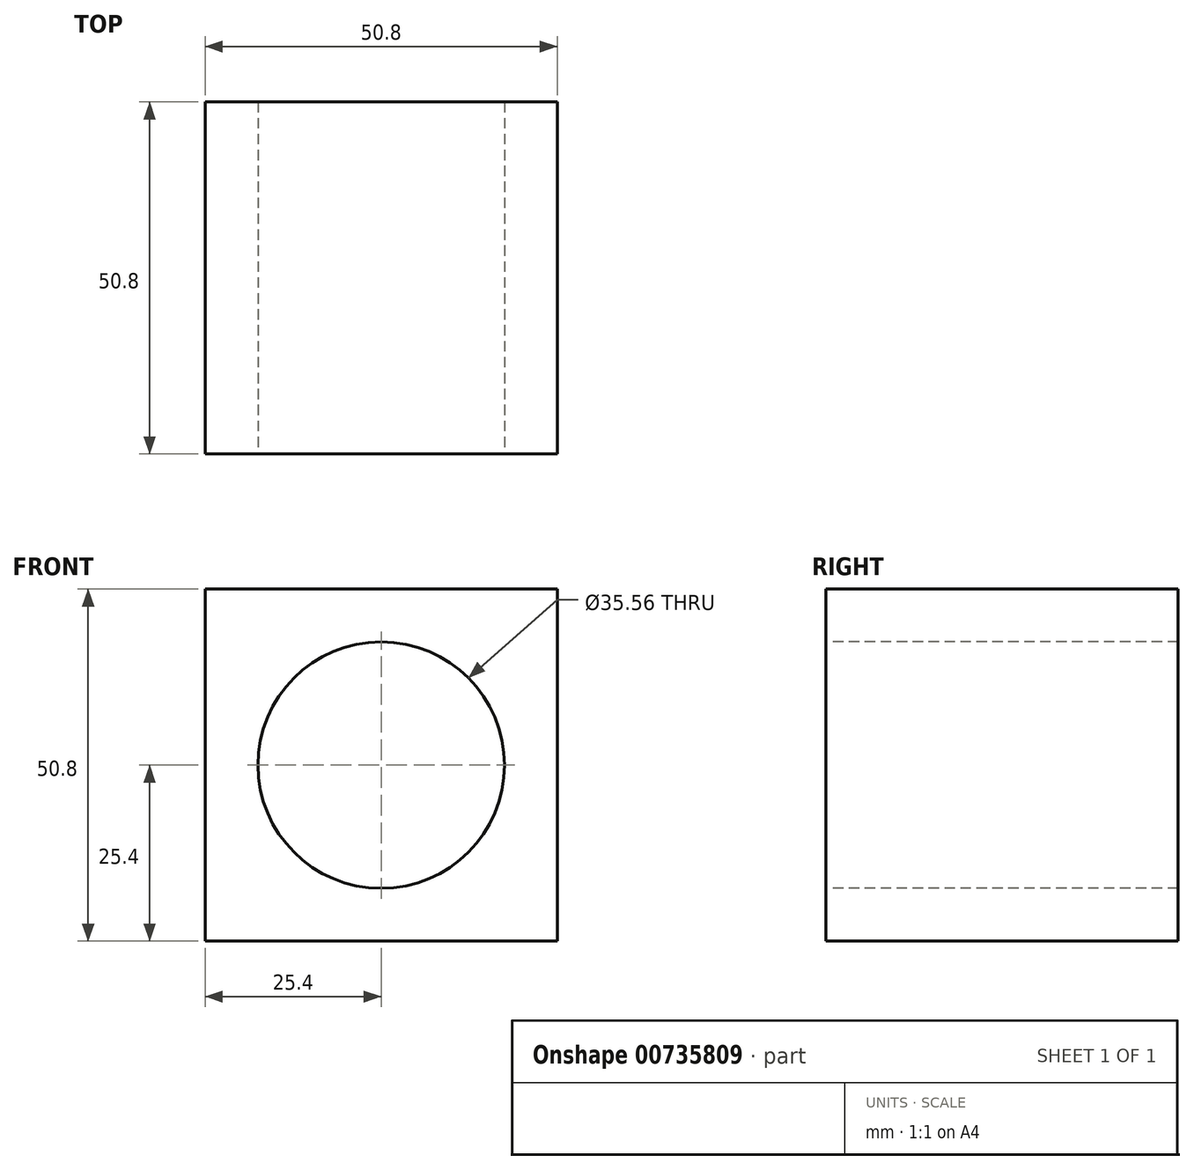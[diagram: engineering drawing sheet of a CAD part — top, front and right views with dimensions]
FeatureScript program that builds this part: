
annotation { "Feature Type Name" : "Feature", "Feature Type Description" : "" }
export const myFeature = defineFeature(function(context is Context, id is Id, definition is map)
    precondition{}
    {
        {
            var Q0;
            Q0=qCreatedBy(makeId("Front.planeOp"),FACE);
            var sketch = newSketch(context, id + "F0", { "sketchPlane" : qUnion([Q0])});
            skLineSegment(sketch, "E0", {"start": v(0, 0) * mm, "end": v(50.8, 0) * mm});
            skLineSegment(sketch, "E1", {"start": v(50.8, 0) * mm, "end": v(50.8, 50.8) * mm});
            skLineSegment(sketch, "E2", {"start": v(50.8, 50.8) * mm, "end": v(0, 50.8) * mm});
            skLineSegment(sketch, "E3", {"start": v(0, 50.8) * mm, "end": v(0, 0) * mm});
            skSolve(sketch);
        }
        {
            var Q0;
            Q0=makeQuery(id+"F0.imprint","IMPRINT",FACE,{"disambiguationData":[TD([[makeQuery(id+"F0.imprint","IMPRINT",EDGE,{"derivedFrom":sQuery(id+"F0.wireOp",EDGE,"E0")}),1.0]])]});
            extrude(context, id + "F1", {"entities" : qUnion([Q0]), "depth" : 50.8 * mm, "offsetDistance" : 25.4 * mm});
        }
        {
            var Q0;
            Q0=makeQuery(id+"F1.opExtrude","CAP_FACE",FACE,{"disambiguationData":[OSD([sQuery(id+"F0.wireOp",EDGE,"E0"),sQuery(id+"F0.wireOp",EDGE,"E1"),sQuery(id+"F0.wireOp",EDGE,"E2"),sQuery(id+"F0.wireOp",EDGE,"E3")])],"isStart":false});
            var sketch = newSketch(context, id + "F2", { "sketchPlane" : qUnion([Q0])});
            skCircle(sketch, "E4", {"center": v(25.4, 25.4) * mm, "radius": 17.78 * mm});
            skSolve(sketch);
        }
        {
            var Q0;
            Q0 = qSketchRegion(id + "F2", true);
            extrude(context, id + "F3", {"entities" : qUnion([Q0]), "operationType" : NewBodyOperationType.REMOVE, "oppositeDirection" : true, "depth" : 50.8 * mm, "offsetDistance" : 25.4 * mm});
        }
    });
